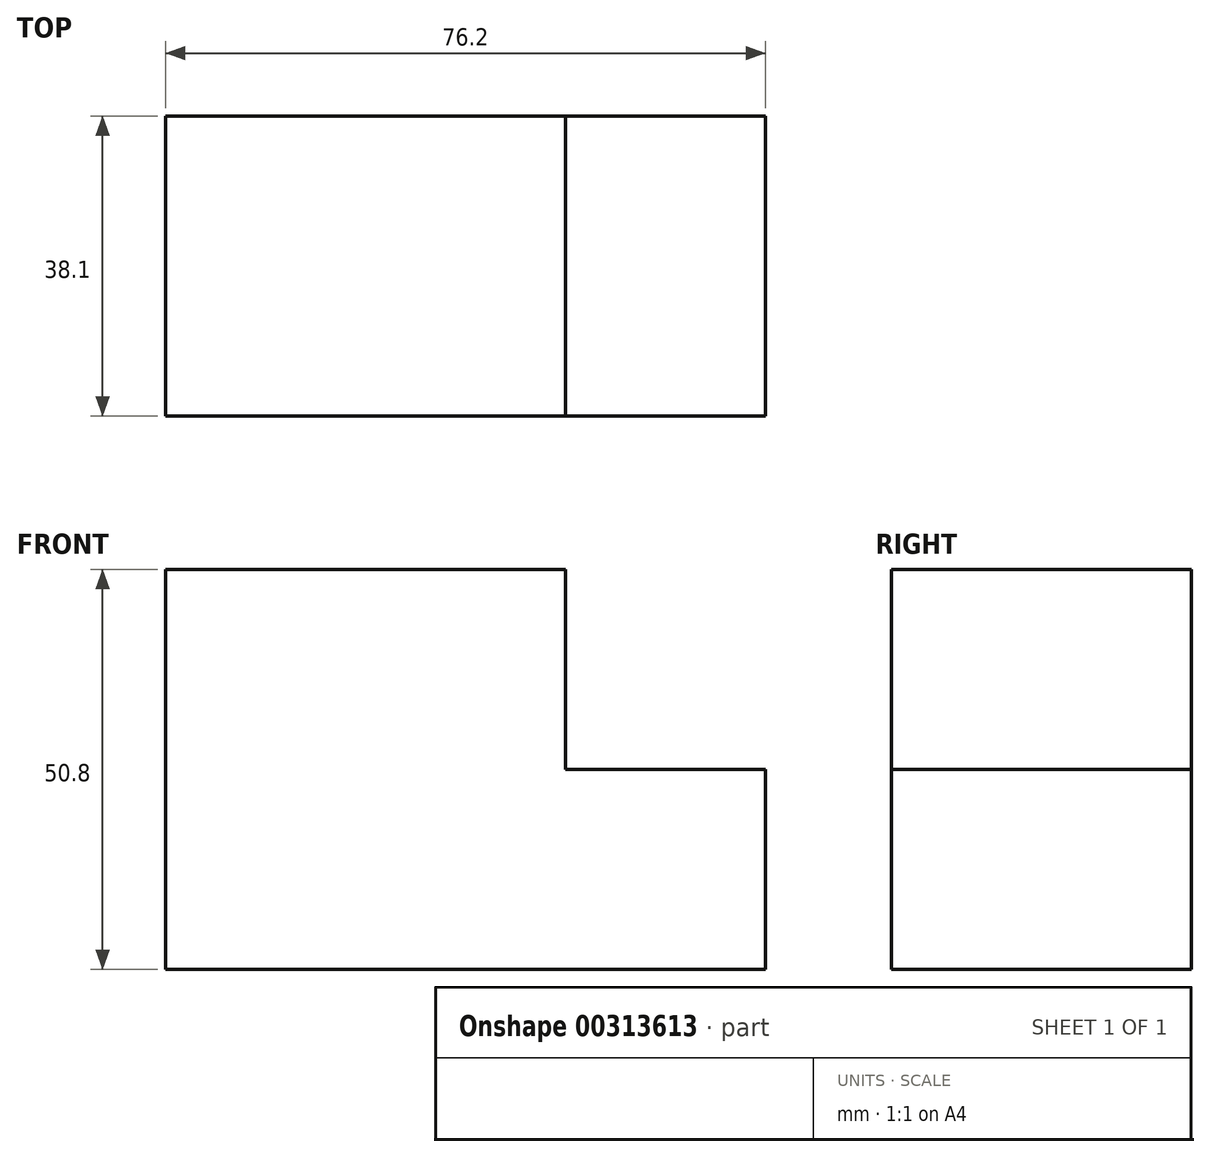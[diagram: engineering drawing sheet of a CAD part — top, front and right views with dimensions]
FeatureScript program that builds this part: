
annotation { "Feature Type Name" : "Feature", "Feature Type Description" : "" }
export const myFeature = defineFeature(function(context is Context, id is Id, definition is map)
    precondition{}
    {
        {
            var Q0;
            Q0=qCreatedBy(makeId("Front.planeOp"),FACE);
            var sketch = newSketch(context, id + "F0", { "sketchPlane" : qUnion([Q0])});
            skLineSegment(sketch, "E0", {"start": v(-40.59, -25.4) * mm, "end": v(35.61, -25.4) * mm});
            skLineSegment(sketch, "E1", {"start": v(35.61, -25.4) * mm, "end": v(35.61, 0) * mm});
            skLineSegment(sketch, "E2", {"start": v(35.61, 0) * mm, "end": v(10.21, 0) * mm});
            skLineSegment(sketch, "E3", {"start": v(10.21, 0) * mm, "end": v(10.21, 25.4) * mm});
            skLineSegment(sketch, "E4", {"start": v(10.21, 25.4) * mm, "end": v(-40.59, 25.4) * mm});
            skLineSegment(sketch, "E5", {"start": v(-40.59, 25.4) * mm, "end": v(-40.59, -25.4) * mm});
            skSolve(sketch);
        }
        {
            var Q0;
            Q0=makeQuery(id+"F0.imprint","IMPRINT",FACE,{"disambiguationData":[TD([[makeQuery(id+"F0.imprint","IMPRINT",EDGE,{"derivedFrom":sQuery(id+"F0.wireOp",EDGE,"E0")}),1.0]])]});
            extrude(context, id + "F1", {"entities" : qUnion([Q0]), "depth" : 38.1 * mm});
        }
    });
